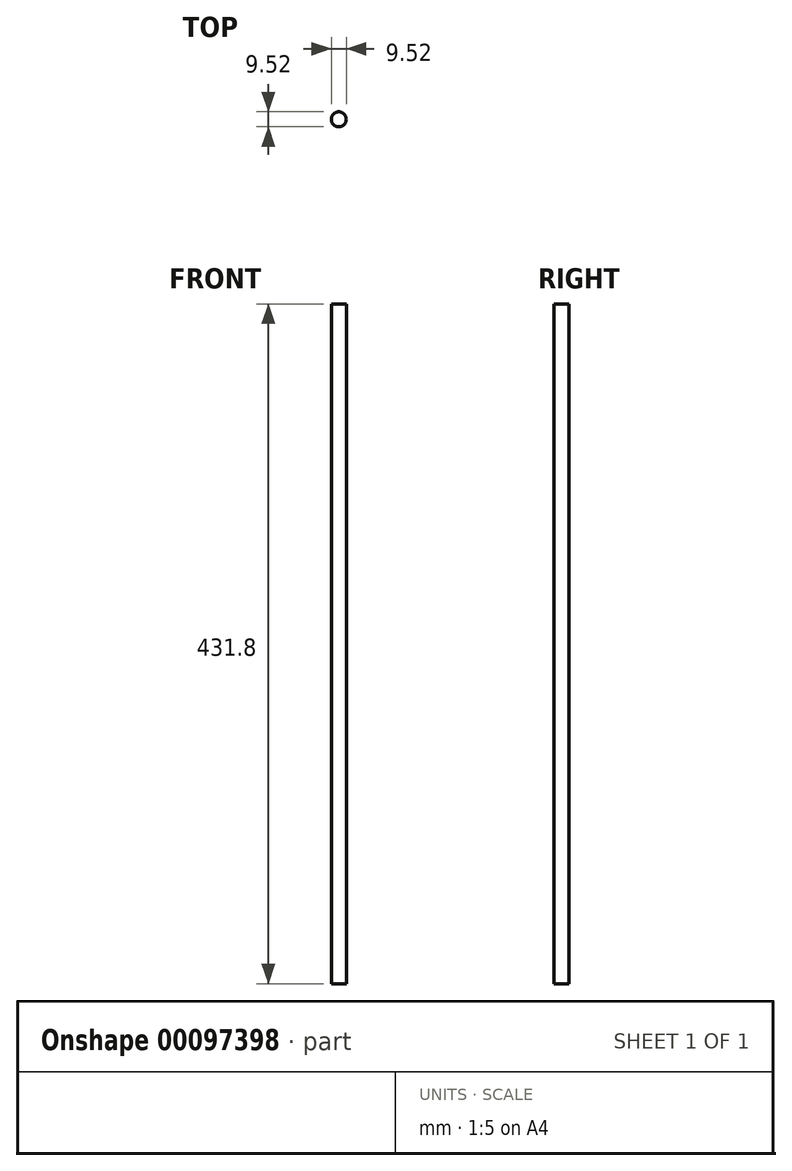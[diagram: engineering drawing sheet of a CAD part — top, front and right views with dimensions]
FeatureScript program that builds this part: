
annotation { "Feature Type Name" : "Feature", "Feature Type Description" : "" }
export const myFeature = defineFeature(function(context is Context, id is Id, definition is map)
    precondition{}
    {
        {
            var Q0;
            Q0=qCreatedBy(makeId("Top.planeOp"),FACE);
            var sketch = newSketch(context, id + "F0", { "sketchPlane" : qUnion([Q0])});
            skCircle(sketch, "E0", {"center": v(0, 0) * mm, "radius": 4.76 * mm});
            skSolve(sketch);
        }
        {
            var Q0;
            Q0=makeQuery(id+"F0.imprint","IMPRINT",FACE,{"disambiguationData":[TD([[makeQuery(id+"F0.imprint","IMPRINT",EDGE,{"derivedFrom":sQuery(id+"F0.wireOp",EDGE,"E0")}),1.0]])]});
            extrude(context, id + "F1", {"entities" : qUnion([Q0]), "depth" : 431.8 * mm});
        }
    });
